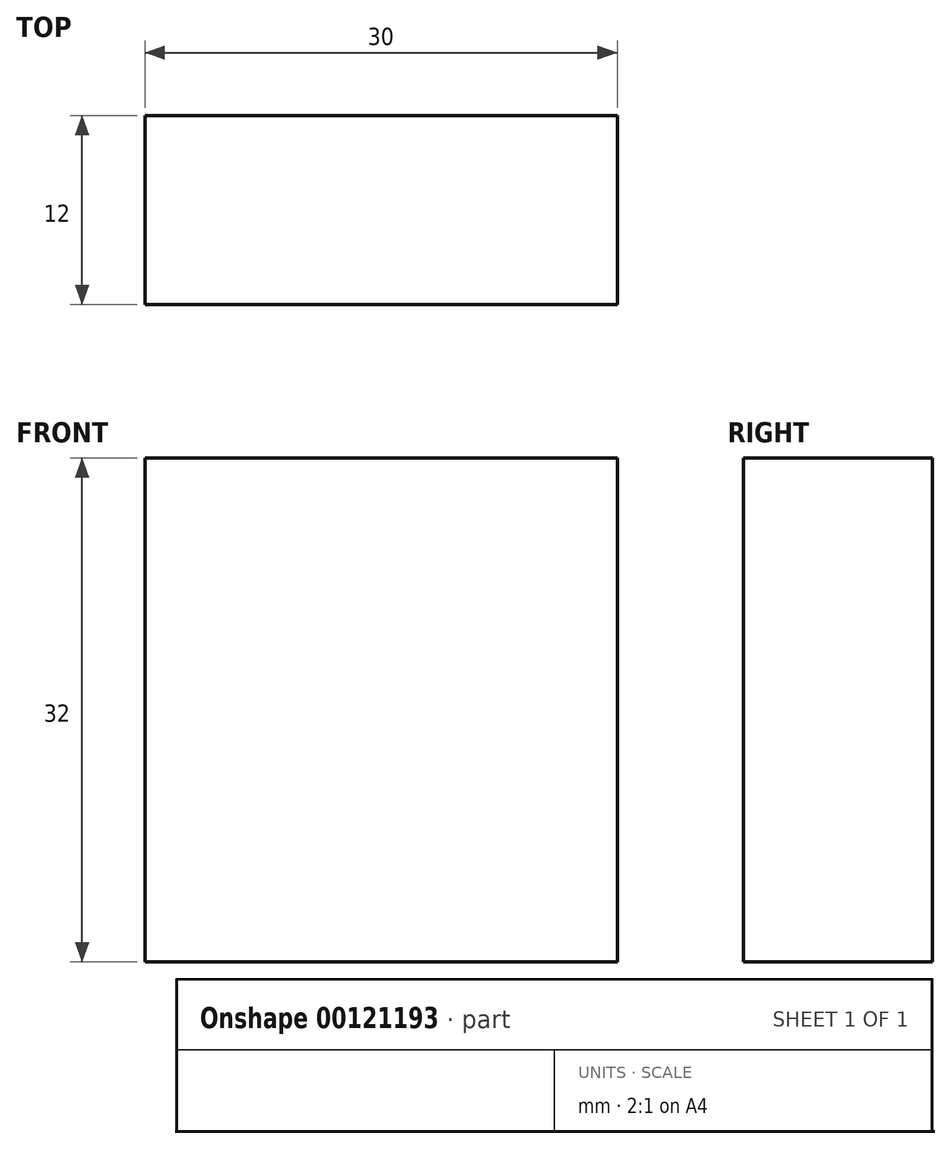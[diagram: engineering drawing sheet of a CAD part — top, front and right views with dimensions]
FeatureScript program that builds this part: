
annotation { "Feature Type Name" : "Feature", "Feature Type Description" : "" }
export const myFeature = defineFeature(function(context is Context, id is Id, definition is map)
    precondition{}
    {
        {
            var Q0;
            Q0=qCreatedBy(makeId("Front.planeOp"),FACE);
            var sketch = newSketch(context, id + "F0", { "sketchPlane" : qUnion([Q0])});
            skLineSegment(sketch, "E0.bottom", {"start": v(15, -16) * mm, "end": v(-15, -16) * mm});
            skLineSegment(sketch, "E0.top", {"start": v(15, 16) * mm, "end": v(-15, 16) * mm});
            skLineSegment(sketch, "E0.left", {"start": v(15, -16) * mm, "end": v(15, 16) * mm});
            skLineSegment(sketch, "E0.right", {"start": v(-15, -16) * mm, "end": v(-15, 16) * mm});
            skPoint(sketch, "E0.middle", {"position": v(0, 0) * mm});
            skSolve(sketch);
        }
        {
            var Q0;
            Q0 = qSketchRegion(id + "F0", true);
            extrude(context, id + "F1", {"entities" : qUnion([Q0]), "depth" : 12 * mm});
        }
    });
